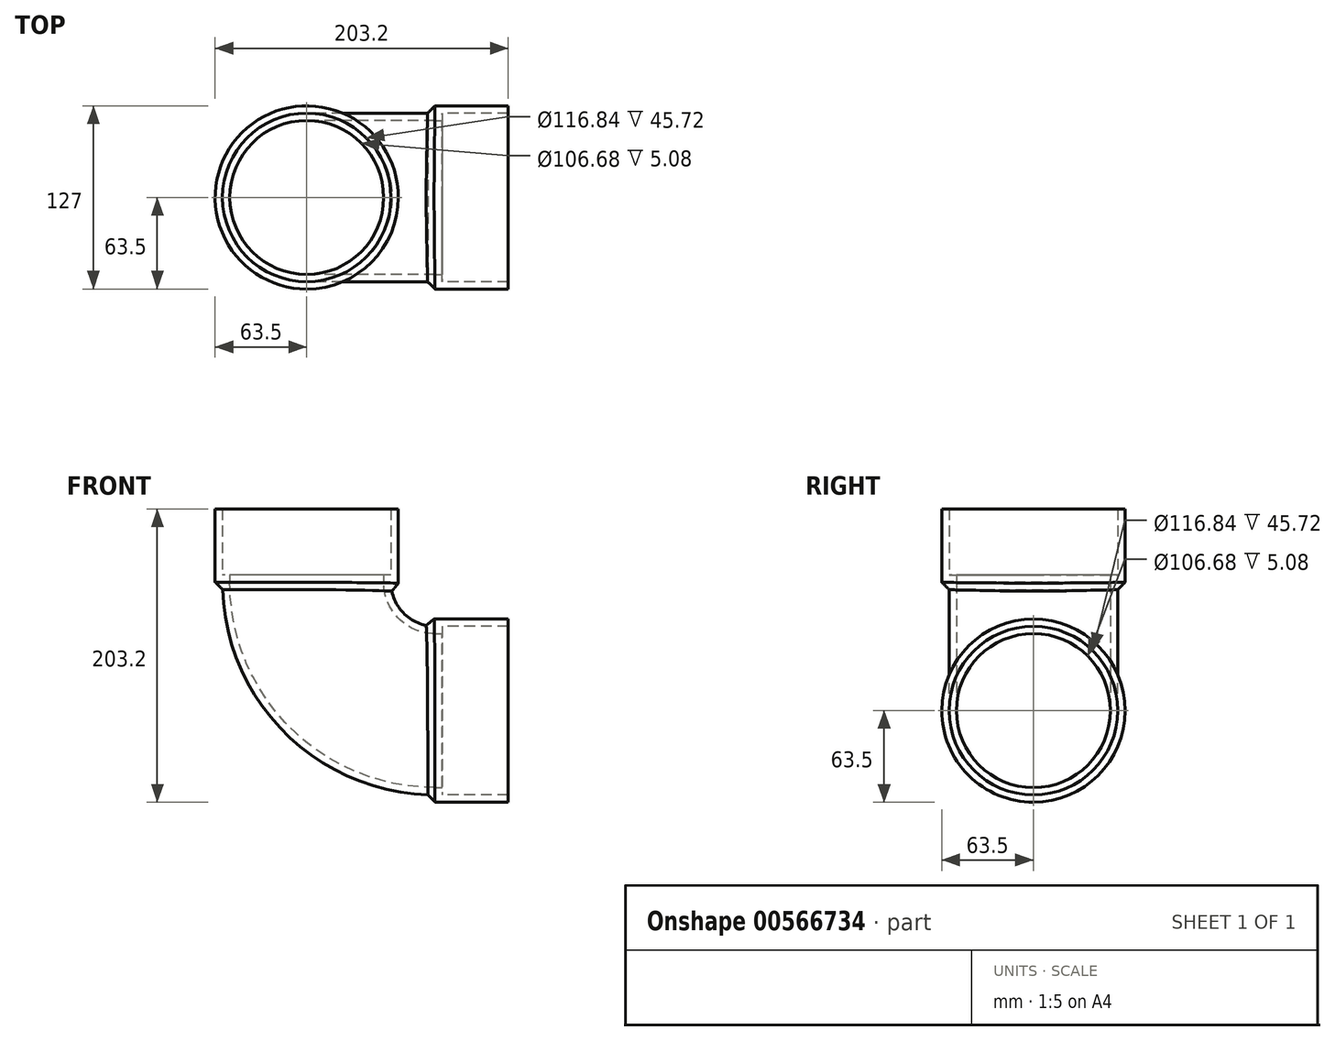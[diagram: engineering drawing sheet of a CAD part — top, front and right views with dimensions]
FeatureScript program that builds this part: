
annotation { "Feature Type Name" : "Feature", "Feature Type Description" : "" }
export const myFeature = defineFeature(function(context is Context, id is Id, definition is map)
    precondition{}
    {
        {
            var Q0;
            Q0=qCreatedBy(makeId("Top.planeOp"),FACE);
            var sketch = newSketch(context, id + "F0", { "sketchPlane" : qUnion([Q0])});
            skCircle(sketch, "E0", {"center": v(0, 0) * mm, "radius": 63.5 * mm});
            skLineSegment(sketch, "E1", {"start": v(88.9, 40) * mm, "end": v(88.9, -35.24) * mm});
            skSolve(sketch);
        }
        {
            var Q0;
            Q0=makeQuery(id+"F0.imprint","IMPRINT",FACE,{"disambiguationData":[TD([[makeQuery(id+"F0.imprint","IMPRINT",EDGE,{"derivedFrom":sQuery(id+"F0.wireOp",EDGE,"E0")}),1.0]])]});
            var Q1;
            Q1=makeQuery(id+"F0.imprint","IMPRINT",FACE,{"disambiguationData":[TD([[makeQuery(id+"F0.imprint","IMPRINT",EDGE,{"derivedFrom":sQuery(id+"F0.wireOp",EDGE,"4vr16HTV-bw5p-N6pc-xBq0-Ipfc8GHGUd3C")}),1.0]])]});
            extrude(context, id + "F1", {"entities" : qUnion([Q0, Q1]), "depth" : 50.8 * mm, "offsetDistance" : 25.4 * mm});
        }
        {
            var Q0;
            Q0=qCreatedBy(makeId("Top.planeOp"),FACE);
            var sketch = newSketch(context, id + "F2", { "sketchPlane" : qUnion([Q0])});
            skCircle(sketch, "E2", {"center": v(0, 0) * mm, "radius": 58.42 * mm});
            skSolve(sketch);
        }
        {
            var Q0;
            Q0=makeQuery(id+"F2.imprint","IMPRINT",FACE,{"disambiguationData":[TD([[makeQuery(id+"F2.imprint","IMPRINT",EDGE,{"derivedFrom":sQuery(id+"F2.wireOp",EDGE,"E2")}),1.0]])]});
            extrude(context, id + "F3", {"entities" : qUnion([Q0]), "operationType" : NewBodyOperationType.REMOVE, "endBound" : BoundingType.SYMMETRIC, "depth" : 101.6 * mm, "offsetDistance" : 25.4 * mm});
        }
        {
            var Q0;
            Q0 = qSketchRegion(id + "F2", true);
            var Q1;
            Q1=sQuery(id+"F0.wireOp",EDGE,"E1");
            revolve(context, id + "F4", {"operationType" : NewBodyOperationType.ADD, "surfaceOperationType" : NewSurfaceOperationType.NEW, "entities" : qUnion([Q0]), "axis" : qUnion([Q1]), "revolveType" : RevolveType.ONE_DIRECTION, "angle" : 90 * degree});
        }
        {
            var Q0;
            Q0=makeQuery(id+"F2.imprint","IMPRINT",FACE,{"disambiguationData":[TD([[makeQuery(id+"F2.imprint","IMPRINT",EDGE,{"derivedFrom":sQuery(id+"F2.wireOp",EDGE,"E2")}),1.0]])]});
            extrude(context, id + "F5", {"entities" : qUnion([Q0]), "operationType" : NewBodyOperationType.ADD, "depth" : 5.08 * mm, "offsetDistance" : 25.4 * mm});
        }
        {
            var Q0;
            Q0=makeQuery(id+"F4.opRevolve","CAP_FACE",FACE,{"disambiguationData":[OSD([sQuery(id+"F2.wireOp",EDGE,"E2")])],"isStart":false});
            var sketch = newSketch(context, id + "F6", { "sketchPlane" : qUnion([Q0])});
            skPoint(sketch, "E3", {"position": v(0, -88.9) * mm});
            skCircle(sketch, "E4", {"center": v(0, -88.9) * mm, "radius": 58.42 * mm});
            skSolve(sketch);
        }
        {
            var Q0;
            Q0=makeQuery(id+"F6.imprint","IMPRINT",FACE,{"disambiguationData":[TD([[makeQuery(id+"F6.imprint","IMPRINT",EDGE,{"derivedFrom":sQuery(id+"F6.wireOp",EDGE,"E4")}),-1.0]])]});
            var sketch = newSketch(context, id + "F7", { "sketchPlane" : qUnion([Q0])});
            skPoint(sketch, "E5", {"position": v(0, -88.9) * mm});
            skCircle(sketch, "E6", {"center": v(0, -88.9) * mm, "radius": 63.5 * mm});
            skSolve(sketch);
        }
        {
            var Q0;
            Q0=makeQuery(id+"F6.imprint","IMPRINT",FACE,{"disambiguationData":[TD([[makeQuery(id+"F6.imprint","IMPRINT",EDGE,{"derivedFrom":sQuery(id+"F6.wireOp",EDGE,"E4")}),-1.0]])]});
            extrude(context, id + "F8", {"entities" : qUnion([Q0]), "operationType" : NewBodyOperationType.ADD, "depth" : 5.08 * mm, "offsetDistance" : 25.4 * mm});
        }
        {
            var Q0;
            Q0=makeQuery(id+"F7.imprint","IMPRINT",FACE,{"disambiguationData":[TD([[makeQuery(id+"F7.imprint","IMPRINT",EDGE,{"derivedFrom":sQuery(id+"F7.wireOp",EDGE,"E6")}),1.0]])]});
            extrude(context, id + "F9", {"entities" : qUnion([Q0]), "operationType" : NewBodyOperationType.ADD, "depth" : 50.8 * mm, "offsetDistance" : 25.4 * mm});
        }
        {
            var Q0;
            Q0=qCreatedBy(makeId("Top.planeOp"),FACE);
            var sketch = newSketch(context, id + "F10", { "sketchPlane" : qUnion([Q0])});
            skCircle(sketch, "E7", {"center": v(0, 0) * mm, "radius": 53.34 * mm});
            skSolve(sketch);
        }
        {
            var Q0;
            Q0 = qSketchRegion(id + "F10", true);
            extrude(context, id + "F11", {"entities" : qUnion([Q0]), "operationType" : NewBodyOperationType.REMOVE, "oppositeDirection" : true, "depth" : -25.4 * mm, "offsetDistance" : 25.4 * mm});
        }
        {
            var Q0;
            Q0 = qSketchRegion(id + "F10", true);
            var Q1;
            Q1=sQuery(id+"F0.wireOp",EDGE,"E1");
            revolve(context, id + "F12", {"operationType" : NewBodyOperationType.REMOVE, "surfaceOperationType" : NewSurfaceOperationType.NEW, "entities" : qUnion([Q0]), "axis" : qUnion([Q1]), "revolveType" : RevolveType.ONE_DIRECTION, "angle" : 90 * degree});
        }
        {
            var Q0;
            Q0=makeQuery(id+"F8.opExtrude","CAP_FACE",FACE,{"disambiguationData":[OSD([sQuery(id+"F6.wireOp",EDGE,"E4")])],"isStart":false});
            var sketch = newSketch(context, id + "F13", { "sketchPlane" : qUnion([Q0])});
            skCircle(sketch, "E8", {"center": v(0, -88.9) * mm, "radius": 53.34 * mm});
            skSolve(sketch);
        }
        {
            var Q0;
            Q0 = qSketchRegion(id + "F13", true);
            extrude(context, id + "F14", {"entities" : qUnion([Q0]), "operationType" : NewBodyOperationType.REMOVE, "oppositeDirection" : true, "depth" : 5.08 * mm, "offsetDistance" : 25.4 * mm});
        }
        {
            var Q0;
            {var subQ0=sQuery(id+"F2.wireOp",EDGE,"E2");Q0=makeQuery(id+"F5.boolean.opBoolean","MERGE",EDGE,{"derivedFrom":[makeQuery(id+"F3.boolean.opBoolean","INTERSECT",EDGE,{"derivedFrom":[makeQuery(id+"F1.opExtrude","CAP_FACE",FACE,{"disambiguationData":[OSD([sQuery(id+"F0.wireOp",EDGE,"E0")])],"isStart":true}),makeQuery(id+"F3.opExtrude","SWEPT_FACE",FACE,{"disambiguationData":[OSD([subQ0])]})]}),makeQuery(id+"F4.opRevolve","CAP_EDGE",EDGE,{"disambiguationData":[OSD([subQ0])],"isStart":true}),makeQuery(id+"F5.opExtrude","CAP_EDGE",EDGE,{"disambiguationData":[OSD([subQ0])],"isStart":true})]});}
            var Q1;
            {var subQ0=sQuery(id+"F6.wireOp",EDGE,"E4");Q1=makeQuery(id+"F9.boolean.opBoolean","MERGE",EDGE,{"derivedFrom":[makeQuery(id+"F8.boolean.opBoolean","MERGE",EDGE,{"derivedFrom":[makeQuery(id+"F4.opRevolve","CAP_EDGE",EDGE,{"disambiguationData":[OSD([sQuery(id+"F2.wireOp",EDGE,"E2")])],"isStart":false}),makeQuery(id+"F8.opExtrude","CAP_EDGE",EDGE,{"disambiguationData":[OSD([subQ0])],"isStart":true})]}),makeQuery(id+"F9.opExtrude","CAP_EDGE",EDGE,{"disambiguationData":[OSD([subQ0])],"isStart":true})]});}
            chamfer(context, id + "F15", {"entities" : qUnion([Q0, Q1]), "width" : 5.08 * mm, "tangentPropagation" : true});
        }
    });
